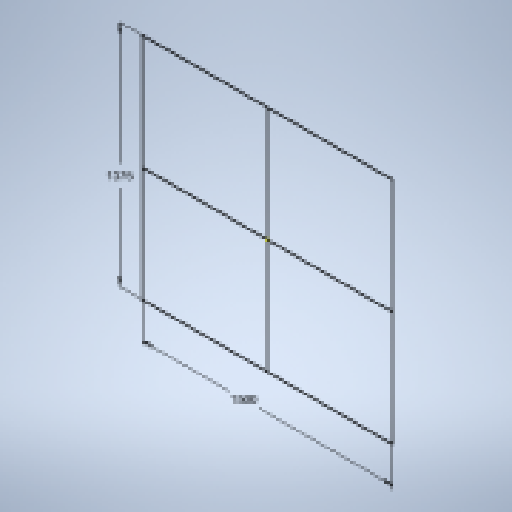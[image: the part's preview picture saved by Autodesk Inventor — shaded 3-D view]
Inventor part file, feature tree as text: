
AUTODESK INVENTOR PART (.ipt)
format: ipt  version: 2025 (Build 290162010, 162A)  size: 129,024 bytes
history: native  units: mm
features: sketch x1
ambient origin geometry x8: Origin, YZ Plane, XZ Plane, XY Plane, X Axis, Y Axis, Z Axis, Center Point
feature tree (1):
  sketch  "Sketch1"  dims[d0=1375.0mm d1=1500.0mm]
